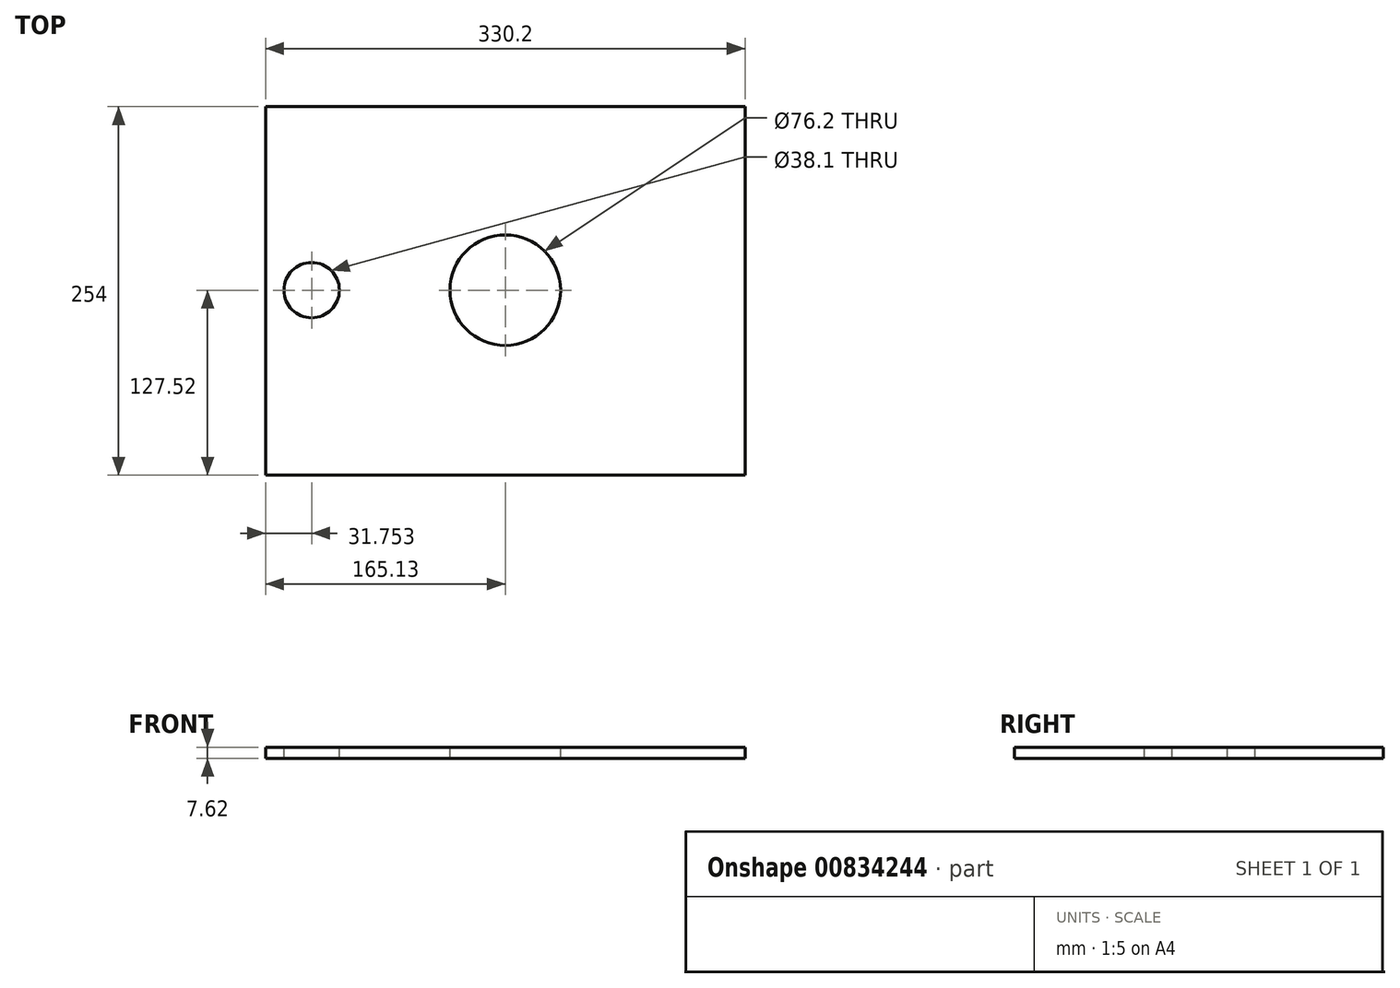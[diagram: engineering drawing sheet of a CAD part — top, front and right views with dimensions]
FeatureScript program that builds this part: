
annotation { "Feature Type Name" : "Feature", "Feature Type Description" : "" }
export const myFeature = defineFeature(function(context is Context, id is Id, definition is map)
    precondition{}
    {
        {
            var Q0;
            Q0=qCreatedBy(makeId("Top.planeOp"),FACE);
            var sketch = newSketch(context, id + "F0", { "sketchPlane" : qUnion([Q0])});
            skLineSegment(sketch, "E0.bottom", {"start": v(165.07, 126.48) * mm, "end": v(-165.13, 126.48) * mm});
            skLineSegment(sketch, "E0.top", {"start": v(165.07, -127.52) * mm, "end": v(-165.13, -127.52) * mm});
            skLineSegment(sketch, "E0.left", {"start": v(165.07, 126.48) * mm, "end": v(165.07, -127.52) * mm});
            skLineSegment(sketch, "E0.right", {"start": v(-165.13, 126.48) * mm, "end": v(-165.13, -127.52) * mm});
            skPoint(sketch, "E0.middle", {"position": v(-0.03, -0.52) * mm});
            skSolve(sketch);
        }
        {
            var Q0;
            Q0=makeQuery(id+"F0.imprint","IMPRINT",FACE,{"disambiguationData":[TD([[makeQuery(id+"F0.imprint","IMPRINT",EDGE,{"derivedFrom":sQuery(id+"F0.wireOp",EDGE,"E0.bottom")}),1.0]])]});
            extrude(context, id + "F1", {"entities" : qUnion([Q0]), "depth" : 7.62 * mm, "offsetDistance" : 25.4 * mm});
        }
        {
            var Q0;
            Q0=makeQuery(id+"F1.opExtrude","CAP_FACE",FACE,{"disambiguationData":[OSD([sQuery(id+"F0.wireOp",EDGE,"E0.bottom"),sQuery(id+"F0.wireOp",EDGE,"E0.top"),sQuery(id+"F0.wireOp",EDGE,"E0.left"),sQuery(id+"F0.wireOp",EDGE,"E0.right")])],"isStart":false});
            var sketch = newSketch(context, id + "F2", { "sketchPlane" : qUnion([Q0])});
            skCircle(sketch, "E1", {"center": v(0, 0) * mm, "radius": 38.1 * mm});
            skSolve(sketch);
        }
        {
            var Q0;
            Q0=makeQuery(id+"F1.opExtrude","CAP_FACE",FACE,{"disambiguationData":[OSD([sQuery(id+"F0.wireOp",EDGE,"E0.bottom"),sQuery(id+"F0.wireOp",EDGE,"E0.top"),sQuery(id+"F0.wireOp",EDGE,"E0.left"),sQuery(id+"F0.wireOp",EDGE,"E0.right")])],"isStart":false});
            var sketch = newSketch(context, id + "F3", { "sketchPlane" : qUnion([Q0])});
            skCircle(sketch, "E2", {"center": v(-133.38, 0) * mm, "radius": 19.05 * mm});
            skSolve(sketch);
        }
        {
            var Q0;
            Q0=makeQuery(id+"F2.imprint","IMPRINT",FACE,{"disambiguationData":[TD([[makeQuery(id+"F2.imprint","IMPRINT",EDGE,{"derivedFrom":sQuery(id+"F2.wireOp",EDGE,"E1")}),1.0]])]});
            var Q1;
            Q1=sQuery(id+"F2.wireOp",EDGE,"E1");
            extrude(context, id + "F4", {"entities" : qUnion([Q0]), "operationType" : NewBodyOperationType.REMOVE, "surfaceEntities" : qUnion([Q1]), "endBound" : BoundingType.THROUGH_ALL, "oppositeDirection" : true, "depth" : 25.4 * mm, "offsetDistance" : 25.4 * mm});
        }
        {
            var Q0;
            Q0=makeQuery(id+"F3.imprint","IMPRINT",FACE,{"disambiguationData":[TD([[makeQuery(id+"F3.imprint","IMPRINT",EDGE,{"derivedFrom":sQuery(id+"F3.wireOp",EDGE,"E2")}),1.0]])]});
            var Q1;
            Q1=sQuery(id+"F3.wireOp",EDGE,"E2");
            extrude(context, id + "F5", {"entities" : qUnion([Q0]), "operationType" : NewBodyOperationType.REMOVE, "surfaceEntities" : qUnion([Q1]), "endBound" : BoundingType.THROUGH_ALL, "oppositeDirection" : true, "depth" : 25.4 * mm, "offsetDistance" : 25.4 * mm});
        }
    });
